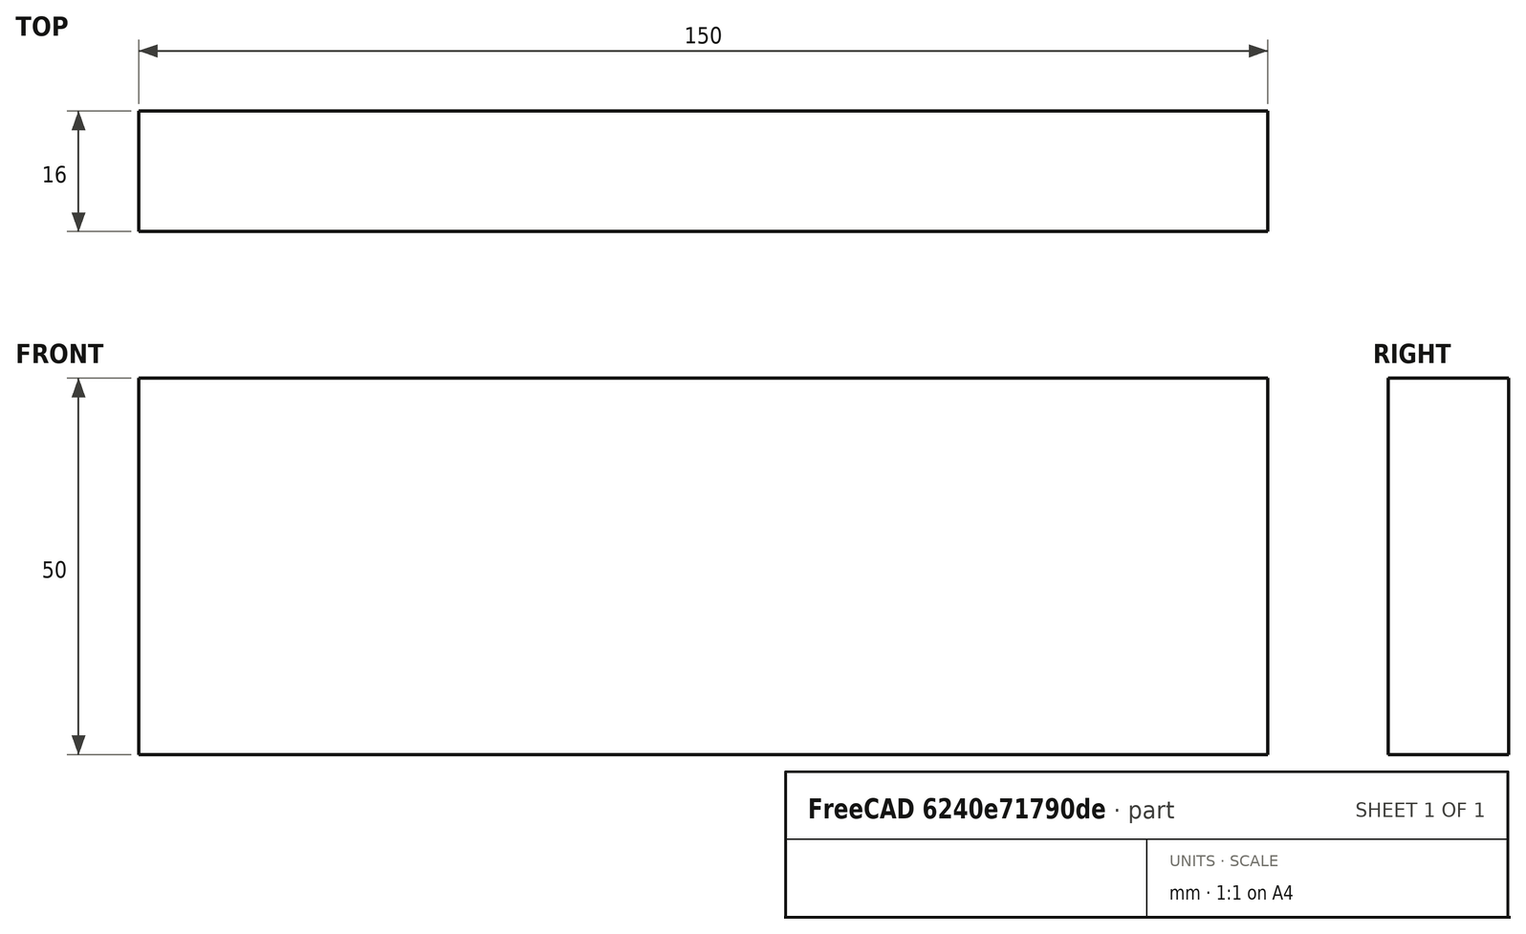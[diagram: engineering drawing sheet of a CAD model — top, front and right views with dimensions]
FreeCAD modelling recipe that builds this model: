
FCSTD DOCUMENT  (FreeCAD 0.15R4671 (Git))
Label: Flat Bar 150x16 EN10058 S235JR
License: All rights reserved
LicenseURL: http://en.wikipedia.org/wiki/All_rights_reserved
objects: Sketcher::SketchObject×1, Part::Extrusion×1
note: 2 computed .brp shape members not serialized (recipe doc carries the construction recipe); baked Part::Feature solids carry a one-line shape summary decoded from their .brp

FEATURE [Sketcher::SketchObject] Sketch
  sketch-geometry (4):
    g0: LineSegment StartX=-75 StartY=-8 StartZ=0 EndX=75 EndY=-8 EndZ=0
    g1: LineSegment StartX=75 StartY=-8 StartZ=0 EndX=75 EndY=8 EndZ=0
    g2: LineSegment StartX=75 StartY=8 StartZ=0 EndX=-75 EndY=8 EndZ=0
    g3: LineSegment StartX=-75 StartY=8 StartZ=0 EndX=-75 EndY=-8 EndZ=0
  constraints (12):
    c: Coincident(g0,g1)
    c: Coincident(g1,g2)
    c: Coincident(g2,g3)
    c: Coincident(g3,g0)
    c: Horizontal(g0)
    c: Horizontal(g2)
    c: Vertical(g1)
    c: Vertical(g3)
    c: Symmetric(g1,g2,g-2)
    c: Symmetric(g0,g1,g-1)
    c: DistanceY(g1) = 16
    c: DistanceX(g0) = 150
FEATURE [Part::Extrusion] Extrude  label="Flat Bar 150x16 EN10058 S235JR"
  Base = -> Sketch
  Dir = (0,0,50)
  Solid = true
